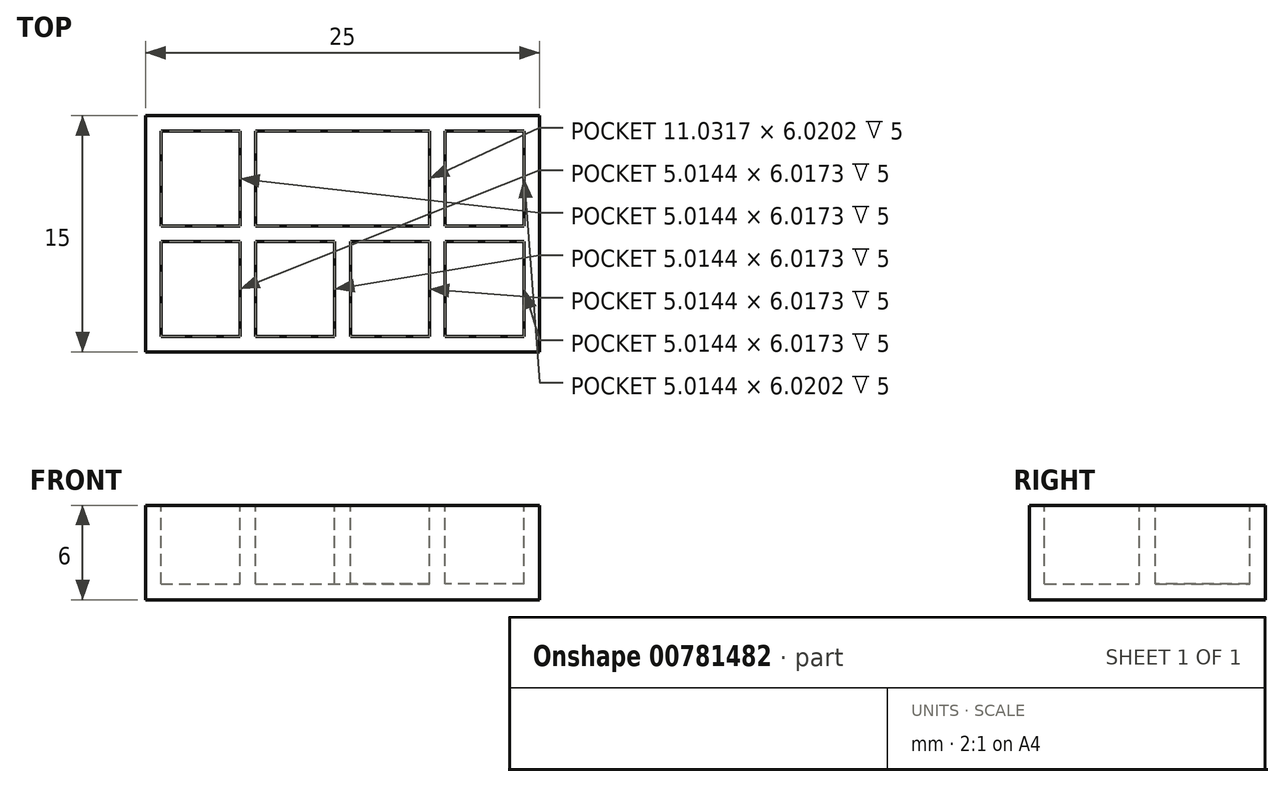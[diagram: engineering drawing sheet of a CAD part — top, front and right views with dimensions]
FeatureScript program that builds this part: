
annotation { "Feature Type Name" : "Feature", "Feature Type Description" : "" }
export const myFeature = defineFeature(function(context is Context, id is Id, definition is map)
    precondition{}
    {
        {
            var Q0;
            Q0=qCreatedBy(makeId("Top.planeOp"),FACE);
            var sketch = newSketch(context, id + "F0", { "sketchPlane" : qUnion([Q0])});
            skLineSegment(sketch, "E0.left", {"start": v(-47.67, 35.37) * mm, "end": v(-47.67, 20.37) * mm});
            skLineSegment(sketch, "E1", {"start": v(-47.67, 20.37) * mm, "end": v(-22.67, 20.37) * mm});
            skLineSegment(sketch, "E2", {"start": v(-22.67, 20.37) * mm, "end": v(-22.67, 35.37) * mm});
            skLineSegment(sketch, "E3", {"start": v(-22.67, 35.37) * mm, "end": v(-47.67, 35.37) * mm});
            skSolve(sketch);
        }
        {
            var Q0;
            Q0=makeQuery(id+"F0.imprint","IMPRINT",FACE,{"disambiguationData":[TD([[makeQuery(id+"F0.imprint","IMPRINT",EDGE,{"derivedFrom":sQuery(id+"F0.wireOp",EDGE,"E0.left")}),1.0]])]});
            extrude(context, id + "F1", {"entities" : qUnion([Q0]), "depth" : 6 * mm, "offsetDistance" : 25.4 * mm});
        }
        {
            var Q0;
            Q0=makeQuery(id+"F1.opExtrude","CAP_FACE",FACE,{"disambiguationData":[OSD([sQuery(id+"F0.wireOp",EDGE,"E0.left"),sQuery(id+"F0.wireOp",EDGE,"E1"),sQuery(id+"F0.wireOp",EDGE,"E2"),sQuery(id+"F0.wireOp",EDGE,"E3")])],"isStart":false});
            var sketch = newSketch(context, id + "F2", { "sketchPlane" : qUnion([Q0])});
            skLineSegment(sketch, "E4", {"start": v(-46.7, 21.35) * mm, "end": v(-46.7, 27.37) * mm});
            skLineSegment(sketch, "E5", {"start": v(-46.7, 34.39) * mm, "end": v(-46.7, 28.37) * mm});
            skLineSegment(sketch, "E6", {"start": v(-46.7, 21.35) * mm, "end": v(-41.69, 21.35) * mm});
            skLineSegment(sketch, "E7", {"start": v(-46.7, 27.37) * mm, "end": v(-41.69, 27.37) * mm});
            skLineSegment(sketch, "E8", {"start": v(-41.69, 27.37) * mm, "end": v(-41.69, 21.35) * mm});
            skLineSegment(sketch, "E9", {"start": v(-46.7, 28.37) * mm, "end": v(-41.69, 28.37) * mm});
            skLineSegment(sketch, "E10", {"start": v(-41.69, 28.37) * mm, "end": v(-41.69, 34.39) * mm});
            skLineSegment(sketch, "E11", {"start": v(-41.69, 34.39) * mm, "end": v(-46.7, 34.39) * mm});
            skLineSegment(sketch, "E12", {"start": v(-40.68, 27.37) * mm, "end": v(-35.67, 27.37) * mm});
            skLineSegment(sketch, "E13", {"start": v(-40.68, 27.37) * mm, "end": v(-40.68, 21.35) * mm});
            skLineSegment(sketch, "E14", {"start": v(-40.68, 21.35) * mm, "end": v(-35.67, 21.35) * mm});
            skLineSegment(sketch, "E15", {"start": v(-35.67, 21.35) * mm, "end": v(-35.67, 27.37) * mm});
            skLineSegment(sketch, "E16", {"start": v(-34.67, 27.37) * mm, "end": v(-34.67, 21.35) * mm});
            skLineSegment(sketch, "E17", {"start": v(-34.67, 21.35) * mm, "end": v(-29.65, 21.35) * mm});
            skLineSegment(sketch, "E18", {"start": v(-23.64, 21.35) * mm, "end": v(-28.65, 21.35) * mm});
            skLineSegment(sketch, "E19", {"start": v(-29.65, 21.35) * mm, "end": v(-29.65, 27.37) * mm});
            skLineSegment(sketch, "E20", {"start": v(-29.65, 27.37) * mm, "end": v(-34.67, 27.37) * mm});
            skLineSegment(sketch, "E21", {"start": v(-28.65, 21.35) * mm, "end": v(-28.65, 27.37) * mm});
            skLineSegment(sketch, "E22", {"start": v(-28.65, 27.37) * mm, "end": v(-23.64, 27.37) * mm});
            skLineSegment(sketch, "E23", {"start": v(-23.64, 27.37) * mm, "end": v(-23.64, 21.35) * mm});
            skLineSegment(sketch, "E24", {"start": v(-28.65, 28.37) * mm, "end": v(-28.65, 34.39) * mm});
            skLineSegment(sketch, "E25", {"start": v(-28.65, 34.39) * mm, "end": v(-23.64, 34.39) * mm});
            skLineSegment(sketch, "E26", {"start": v(-23.64, 34.39) * mm, "end": v(-23.64, 28.37) * mm});
            skLineSegment(sketch, "E27", {"start": v(-23.64, 28.37) * mm, "end": v(-28.65, 28.37) * mm});
            skLineSegment(sketch, "E28", {"start": v(-29.65, 28.37) * mm, "end": v(-29.65, 34.39) * mm});
            skLineSegment(sketch, "E29", {"start": v(-29.65, 34.39) * mm, "end": v(-40.68, 34.39) * mm});
            skLineSegment(sketch, "E30", {"start": v(-40.68, 34.39) * mm, "end": v(-40.68, 28.37) * mm});
            skLineSegment(sketch, "E31", {"start": v(-40.68, 28.37) * mm, "end": v(-29.65, 28.37) * mm});
            skSolve(sketch);
        }
        {
            var Q0;
            Q0=makeQuery(id+"F2.imprint","IMPRINT",FACE,{"disambiguationData":[TD([[makeQuery(id+"F2.imprint","IMPRINT",EDGE,{"derivedFrom":sQuery(id+"F2.wireOp",EDGE,"E28")}),1.0]])]});
            var Q1;
            Q1=makeQuery(id+"F2.imprint","IMPRINT",FACE,{"disambiguationData":[TD([[makeQuery(id+"F2.imprint","IMPRINT",EDGE,{"derivedFrom":sQuery(id+"F2.wireOp",EDGE,"E4")}),-1.0]])]});
            var Q2;
            Q2=makeQuery(id+"F2.imprint","IMPRINT",FACE,{"disambiguationData":[TD([[makeQuery(id+"F2.imprint","IMPRINT",EDGE,{"derivedFrom":sQuery(id+"F2.wireOp",EDGE,"E5")}),1.0]])]});
            var Q3;
            Q3=makeQuery(id+"F2.imprint","IMPRINT",FACE,{"disambiguationData":[TD([[makeQuery(id+"F2.imprint","IMPRINT",EDGE,{"derivedFrom":sQuery(id+"F2.wireOp",EDGE,"E12")}),-1.0]])]});
            var Q4;
            Q4=makeQuery(id+"F2.imprint","IMPRINT",FACE,{"disambiguationData":[TD([[makeQuery(id+"F2.imprint","IMPRINT",EDGE,{"derivedFrom":sQuery(id+"F2.wireOp",EDGE,"E16")}),1.0]])]});
            var Q5;
            Q5=makeQuery(id+"F2.imprint","IMPRINT",FACE,{"disambiguationData":[TD([[makeQuery(id+"F2.imprint","IMPRINT",EDGE,{"derivedFrom":sQuery(id+"F2.wireOp",EDGE,"E18")}),-1.0]])]});
            var Q6;
            Q6=makeQuery(id+"F2.imprint","IMPRINT",FACE,{"disambiguationData":[TD([[makeQuery(id+"F2.imprint","IMPRINT",EDGE,{"derivedFrom":sQuery(id+"F2.wireOp",EDGE,"E24")}),-1.0]])]});
            extrude(context, id + "F3", {"entities" : qUnion([Q0, Q1, Q2, Q3, Q4, Q5, Q6]), "operationType" : NewBodyOperationType.REMOVE, "oppositeDirection" : true, "depth" : 5 * mm, "offsetDistance" : 25.4 * mm});
        }
    });
